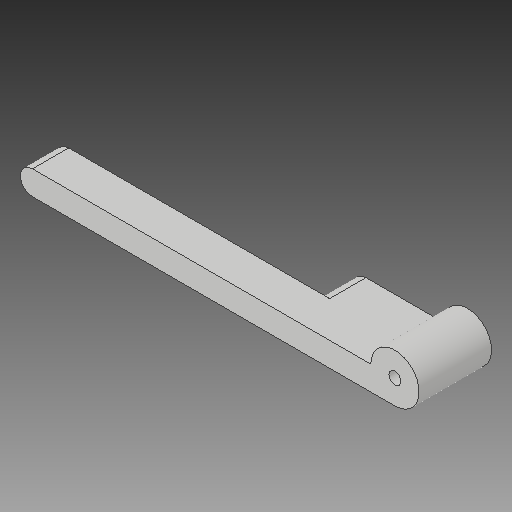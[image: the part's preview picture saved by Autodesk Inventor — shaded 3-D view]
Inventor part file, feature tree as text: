
AUTODESK INVENTOR PART (.ipt)
format: ipt  version: 2017 (Build 210142000, 142)  size: 95,744 bytes
history: native  units: mm
features: other x3, sketch x3
ambient origin geometry x8: Origin, YZ Plane, XZ Plane, XY Plane, X Axis, Y Axis, Z Axis, Center Point
bodies: Solid1 (feature_tree)
feature tree (6):
  other  "Traba.ipt"
  other  "Solid1::Traba.ipt"
  other  "TaggingFeature1"
  sketch  "Sketch1"  dims[d0=10.0mm]
  sketch  "Sketch2"
  sketch  "Sketch3"
